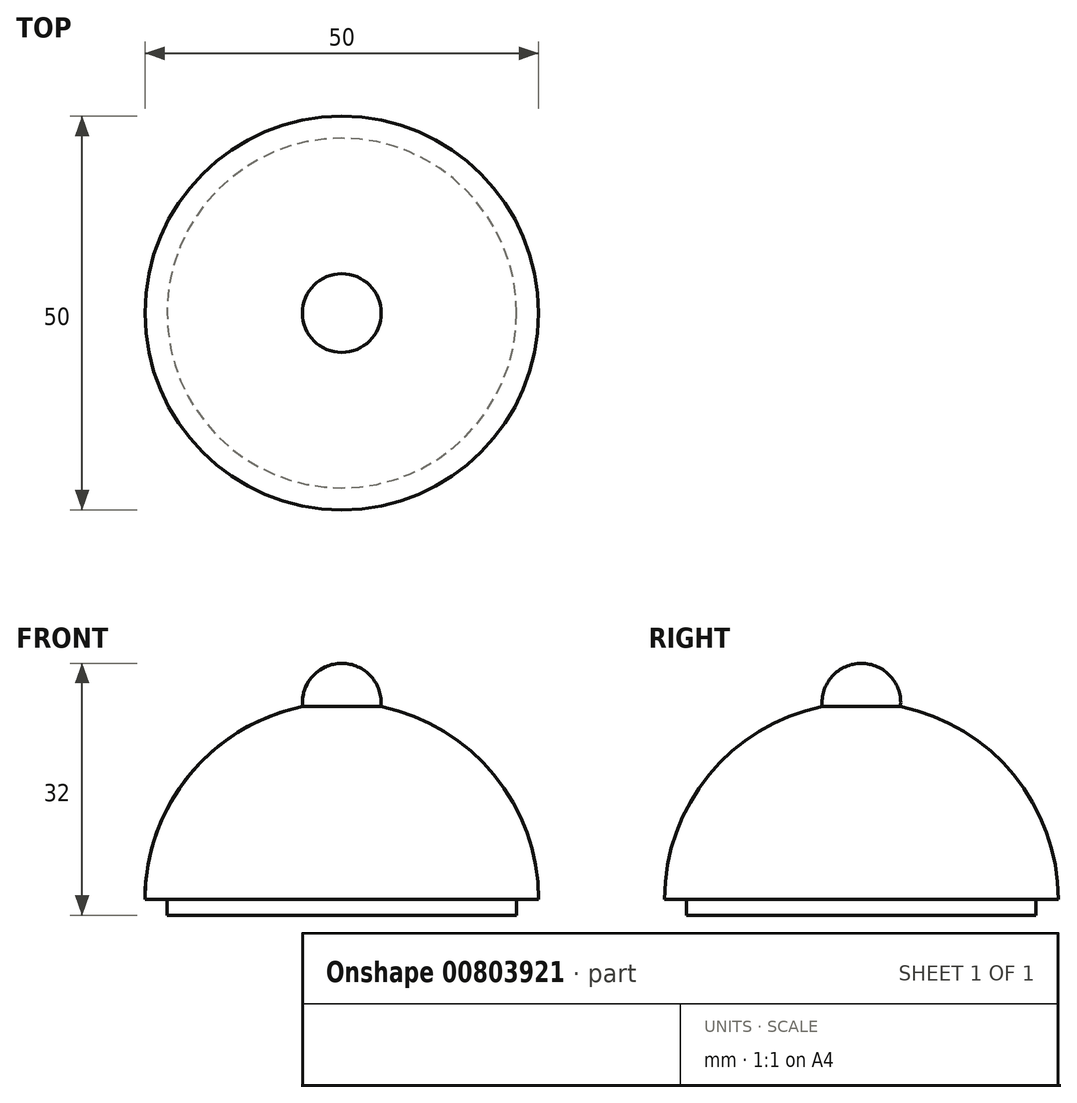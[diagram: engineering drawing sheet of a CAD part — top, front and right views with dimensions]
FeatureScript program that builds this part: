
annotation { "Feature Type Name" : "Feature", "Feature Type Description" : "" }
export const myFeature = defineFeature(function(context is Context, id is Id, definition is map)
    precondition{}
    {
        {
            var Q0;
            Q0=qCreatedBy(makeId("Front.planeOp"),FACE);
            var sketch = newSketch(context, id + "F0", { "sketchPlane" : qUnion([Q0])});
            skArc(sketch, "E0", {"start": v(-4.97, 24.5) * mm, "mid": v(-19.36, 15.82) * mm, "end": v(-25, 0) * mm});
            skLineSegment(sketch, "E1", {"start": v(-25, 0) * mm, "end": v(-22.2, 0) * mm});
            skLineSegment(sketch, "E2", {"start": v(0, 0) * mm, "end": v(0, 25) * mm});
            skLineSegment(sketch, "E3.top", {"start": v(0, -2) * mm, "end": v(-22.2, -2) * mm});
            skLineSegment(sketch, "E3.left", {"start": v(0, 0) * mm, "end": v(0, -2) * mm});
            skLineSegment(sketch, "E3.right", {"start": v(-22.2, 0) * mm, "end": v(-22.2, -2) * mm});
            skArc(sketch, "E4", {"start": v(0, 30) * mm, "mid": v(-3.7, 28.35) * mm, "end": v(-4.97, 24.5) * mm});
            skLineSegment(sketch, "E5", {"start": v(0, 25) * mm, "end": v(0, 30) * mm});
            skSolve(sketch);
        }
        {
            var Q0;
            Q0=makeQuery(id+"F0.imprint","IMPRINT",FACE,{"disambiguationData":[TD([[makeQuery(id+"F0.imprint","IMPRINT",EDGE,{"derivedFrom":sQuery(id+"F0.wireOp",EDGE,"E0")}),1.0]])]});
            var Q1;
            Q1=sQuery(id+"F0.wireOp",EDGE,"E2");
            revolve(context, id + "F1", {"surfaceOperationType" : NewSurfaceOperationType.NEW, "entities" : qUnion([Q0]), "axis" : qUnion([Q1]), "revolveType" : RevolveType.FULL});
        }
    });
